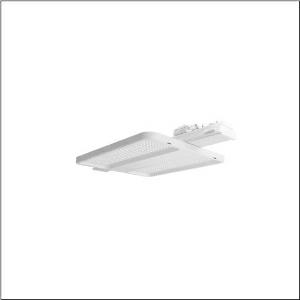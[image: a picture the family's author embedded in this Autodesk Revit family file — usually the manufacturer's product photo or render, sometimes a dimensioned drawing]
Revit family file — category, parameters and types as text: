
# Revit family: highbay_11_fur_licross_tragschiene_midi_51hn12da4mla
name_source: partatom
category: Lighting Fixtures
units: mm (PartAtom-declared; Revit-internal decimal feet)

## family parameters
Cut with Voids When Loaded = No
Host = Face
Light Source = No
Part Type = Normal
Room Calculation Point = No
Round Connector Dimension = Use Diameter
Shared = No

## types (1)
- --- (1 x LED, 28000 lm, 146.6 W, 4000K)
    Apparent Load = 147 VA
    CIE Flux Codes = 87 98 100 100 100
    Color Rendering = 80
    Color Temperature = 4000K
    Default Elevation = 1800 mm
    Description = high bay luminaire Highbay 11 for Licross trunking rail midi; direct symmetric wide distribution, light control with lens of PMMA; UGR ≤ 22 (X = 4H | Y = 8H | S = 0.25H | reflection values 70/50/20); luminous flux: 28.000lm; light colour: 840, colour temperature: 4000K, MacAdam ≤ 2 SDCM (initial), colour rendering: CRI > 80; luminous efficacy: 191lm/W; rated service life: 100.000h (L95) at AT= 25°C; control: DALI 2; luminaire connection: plug, 5-pole, with phase selectionmains connection: 230..240V, AC 50/60Hz; connected load: 146,6W; protection rating (complete): IP64; insulation class (complete): insulation class I (protective earthing); protection symbol: D; impact resistance: IK06; certification: CE, ENEC, VDE, UKCA; internal wiring halogen-free; luminaire LABS conformity tested according to VDMA 24364:2018-05; Suitable for use in the food industry according to the specifications of IFS-Food, HACCP and/or BRC; housing frame of high-performance plastic PA6, matt traffic white (RAL 9016); cover of PMMA; fixing on rail side of steel, galvanised, white; blank cover of PC/ABS, traffic white (RAL 9016); dimension (LxWxH): 750 x 442 x 71mm; permissible operating ambient temperature: -40..+50°C (reducing of maximum allowable ambient temperature of 5°C with ceiling mounting); packaging unit: 1 piece
    Height = 72 mm  [stored 0.23622 ft]
    Lamp = 1 x LED
    Lamp Light Flux = 28000 lm
    Lamp Power = 146.6 W
    Lamp count = 1
    Length = 474 mm
    Luminous efficacy = 191 lm/W
    Manufacturer = Siteco
    ModVariant = No
    Model = 51HN12DA4MLA
    Mounting Place = Ceiling
    Mounting Type = Pendant
    Number of Poles = 1
    OnlyDefault = Yes
    Power Factor = 1
    Product Name = Highbay 11 für Licross Tragschiene midi
    Product group = high bay luminaire
    ProductGroupID = 902
    Protection Class = Protection class I
    Protection Degree = IP 64
    RLX_Detail_Level = 1
    RLX_Emergency_Light_Flux = 0 lm
    RLX_Emergency_Type = 0
    RLX_Emergency_Type_DB = No
    RlxData = <blob elided: 17105 chars, md5=2b270c36>
    Socket = socket
    Standby Power = 0 W
    System Light Flux = 28001 lm
    System Power = 147 W
    Type Comments = factory setting: luminous flux: 100 % | dim-lin: 254 | 661 mA
    Type Image = l_1363258.jpg
    URL = http://relux.com
    VarID = @adj_027203
    Voltage = 0 V
    Weight = 0.00 kg
    Width = 442 mm

note: [stored X ft] marks values corroborated as IEEE doubles in the binary element streams (Revit-internal decimal feet)

## geometry (parser evidence)
native form markers: Blend x4, Sweep x9
no freeform markers — native parametric forms only
